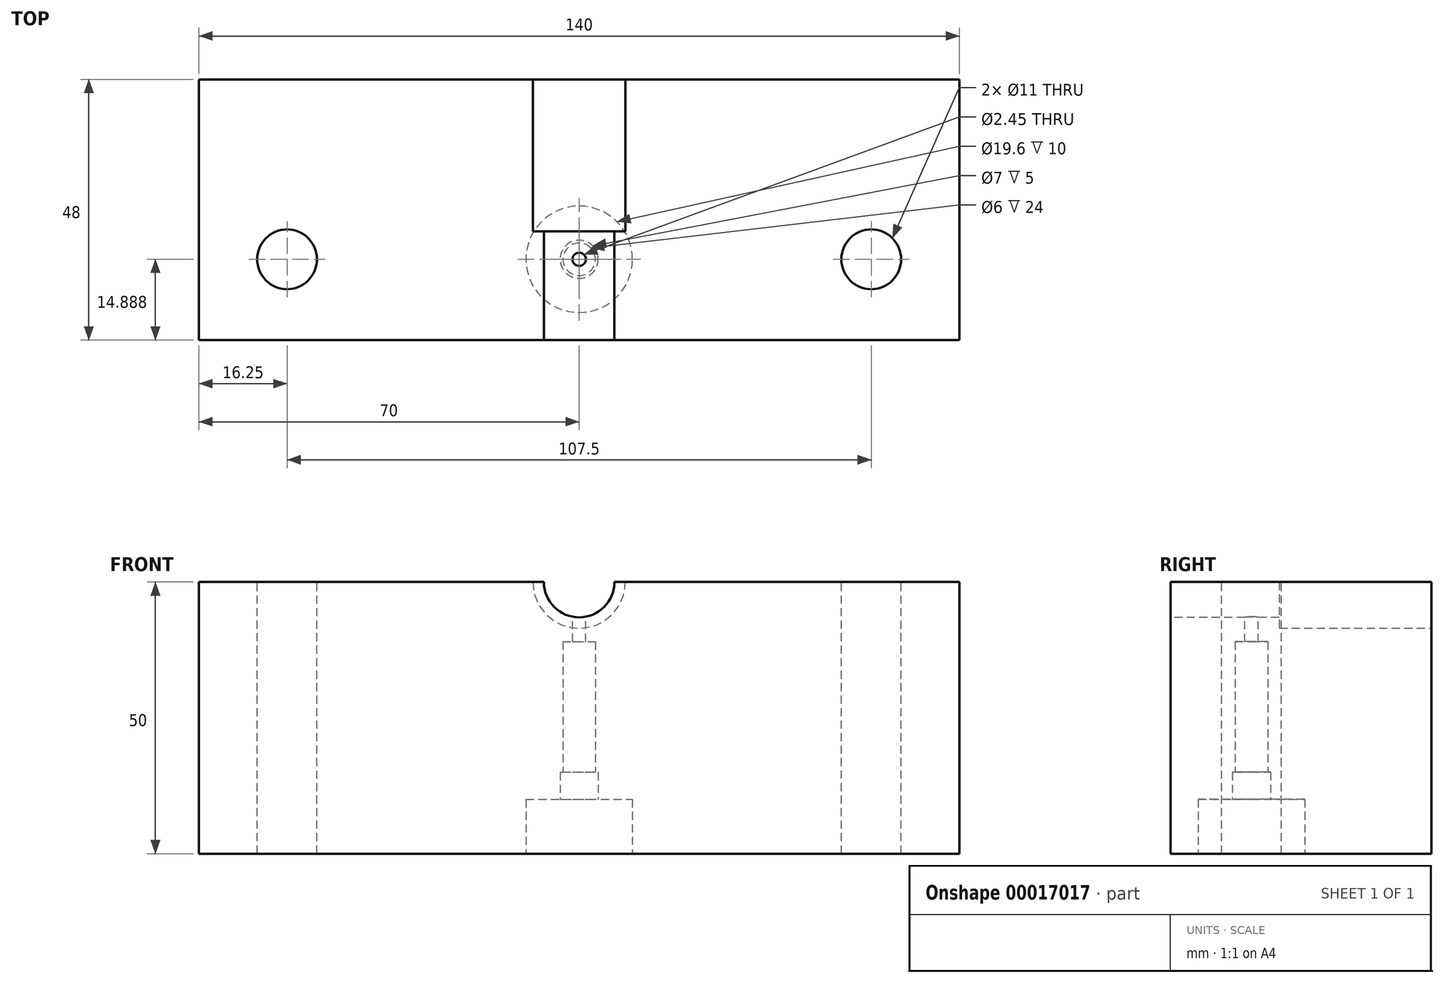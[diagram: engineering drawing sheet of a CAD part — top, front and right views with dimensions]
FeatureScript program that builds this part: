
annotation { "Feature Type Name" : "Feature", "Feature Type Description" : "" }
export const myFeature = defineFeature(function(context is Context, id is Id, definition is map)
    precondition{}
    {
        {
            var Q0;
            Q0=qCreatedBy(makeId("Front.planeOp"),FACE);
            var sketch = newSketch(context, id + "F0", { "sketchPlane" : qUnion([Q0])});
            skLineSegment(sketch, "E0.bottom", {"start": v(0, 0) * mm, "end": v(-140, 0) * mm});
            skLineSegment(sketch, "E0.top", {"start": v(0, 50) * mm, "end": v(-63.5, 50) * mm});
            skLineSegment(sketch, "E0.left", {"start": v(0, 0) * mm, "end": v(0, 50) * mm});
            skLineSegment(sketch, "E0.right", {"start": v(-140, 0) * mm, "end": v(-140, 50) * mm});
            skLineSegment(sketch, "E1.trimOffspring", {"start": v(-76.5, 50) * mm, "end": v(-140, 50) * mm});
            skPoint(sketch, "E2.center.orphan", {"position": v(-70, 50) * mm});
            skLineSegment(sketch, "E3", {"start": v(-63.5, 50) * mm, "end": v(-76.5, 50) * mm});
            skSolve(sketch);
        }
        {
            var Q0;
            Q0=makeQuery(id+"F0.imprint","IMPRINT",FACE,{"disambiguationData":[TD([[makeQuery(id+"F0.imprint","IMPRINT",EDGE,{"derivedFrom":sQuery(id+"F0.wireOp",EDGE,"E0.bottom")}),-1.0]])]});
            extrude(context, id + "F1", {"entities" : qUnion([Q0]), "depth" : 48 * mm});
        }
        {
            var Q0;
            Q0=makeQuery(id+"F1.opExtrude","SWEPT_FACE",FACE,{"disambiguationData":[OSD([sQuery(id+"F0.wireOp",EDGE,"E1.trimOffspring")])]});
            var sketch = newSketch(context, id + "F2", { "sketchPlane" : qUnion([Q0])});
            skCircle(sketch, "E4", {"center": v(-123.75, -33.11) * mm, "radius": 5.5 * mm});
            skCircle(sketch, "E5", {"center": v(-16.25, -33.11) * mm, "radius": 5.5 * mm});
            skSolve(sketch);
        }
        {
            var Q0;
            Q0 = qSketchRegion(id + "F2", true);
            extrude(context, id + "F3", {"entities" : qUnion([Q0]), "operationType" : NewBodyOperationType.REMOVE, "endBound" : BoundingType.THROUGH_ALL, "oppositeDirection" : true, "depth" : 25 * mm});
        }
        {
            var Q0;
            Q0=makeQuery(id+"F1.opExtrude","CAP_FACE",FACE,{"disambiguationData":[OSD([sQuery(id+"F0.wireOp",EDGE,"E0.bottom"),sQuery(id+"F0.wireOp",EDGE,"E0.top"),sQuery(id+"F0.wireOp",EDGE,"E0.left"),sQuery(id+"F0.wireOp",EDGE,"E0.right"),sQuery(id+"F0.wireOp",EDGE,"E1.trimOffspring"),sQuery(id+"F0.wireOp",EDGE,"E3")])],"isStart":false});
            var sketch = newSketch(context, id + "F4", { "sketchPlane" : qUnion([Q0])});
            skCircle(sketch, "E6", {"center": v(-70, 50) * mm, "radius": 6.5 * mm});
            skSolve(sketch);
        }
        {
            var Q0;
            Q0 = qSketchRegion(id + "F4", true);
            extrude(context, id + "F5", {"entities" : qUnion([Q0]), "operationType" : NewBodyOperationType.REMOVE, "oppositeDirection" : true, "depth" : 20 * mm});
        }
        {
            var Q0;
            Q0=makeQuery(id+"F1.opExtrude","CAP_FACE",FACE,{"disambiguationData":[OSD([sQuery(id+"F0.wireOp",EDGE,"E0.bottom"),sQuery(id+"F0.wireOp",EDGE,"E0.top"),sQuery(id+"F0.wireOp",EDGE,"E0.left"),sQuery(id+"F0.wireOp",EDGE,"E0.right"),sQuery(id+"F0.wireOp",EDGE,"E1.trimOffspring"),sQuery(id+"F0.wireOp",EDGE,"E3")])],"isStart":true});
            var sketch = newSketch(context, id + "F6", { "sketchPlane" : qUnion([Q0])});
            skCircle(sketch, "E7", {"center": v(70, 50) * mm, "radius": 8.5 * mm});
            skSolve(sketch);
        }
        {
            var Q0;
            Q0 = qSketchRegion(id + "F6", true);
            extrude(context, id + "F7", {"entities" : qUnion([Q0]), "operationType" : NewBodyOperationType.REMOVE, "oppositeDirection" : true, "depth" : 28 * mm});
        }
        {
            var Q0;
            {var subQ0=sQuery(id+"F0.wireOp",EDGE,"E0.top");var subQ1=sQuery(id+"F0.wireOp",EDGE,"E1.trimOffspring");var subQ2=sQuery(id+"F0.wireOp",EDGE,"E3");var subQ5=sQuery(id+"F0.wireOp",EDGE,"E0.left");Q0=makeQuery(id+"F7.boolean.opBoolean","SPLIT",FACE,{"disambiguationData":[TD([makeQuery(id+"F1.opExtrude","SWEPT_FACE",FACE,{"disambiguationData":[OSD([subQ5])]})])],"derivedFrom":makeQuery(id+"F1.opExtrude","SWEPT_FACE",FACE,{"disambiguationData":[OSD([subQ0,subQ1,subQ2])]})});}
            var sketch = newSketch(context, id + "F8", { "sketchPlane" : qUnion([Q0])});
            skCircle(sketch, "E8", {"center": v(-70, -33.11) * mm, "radius": 1.23 * mm});
            skSolve(sketch);
        }
        {
            var Q0;
            Q0 = qSketchRegion(id + "F8", true);
            extrude(context, id + "F9", {"entities" : qUnion([Q0]), "operationType" : NewBodyOperationType.REMOVE, "endBound" : BoundingType.THROUGH_ALL, "oppositeDirection" : true, "depth" : 25 * mm});
        }
        {
            var Q0;
            Q0=makeQuery(id+"F1.opExtrude","SWEPT_FACE",FACE,{"disambiguationData":[OSD([sQuery(id+"F0.wireOp",EDGE,"E0.bottom")])]});
            var sketch = newSketch(context, id + "F10", { "sketchPlane" : qUnion([Q0])});
            skCircle(sketch, "E9", {"center": v(-70, 33.11) * mm, "radius": 9.8 * mm});
            skSolve(sketch);
        }
        {
            var Q0;
            Q0 = qSketchRegion(id + "F10", true);
            extrude(context, id + "F11", {"entities" : qUnion([Q0]), "operationType" : NewBodyOperationType.REMOVE, "oppositeDirection" : true, "depth" : 10 * mm});
        }
        {
            var Q0;
            Q0=makeQuery(id+"F11.boolean.opBoolean","COPY",FACE,{"derivedFrom":makeQuery(id+"F11.opExtrude","CAP_FACE",FACE,{"disambiguationData":[OSD([sQuery(id+"F10.wireOp",EDGE,"E9")])],"isStart":false})});
            var sketch = newSketch(context, id + "F12", { "sketchPlane" : qUnion([Q0])});
            skCircle(sketch, "E10", {"center": v(-70, 33.11) * mm, "radius": 3.5 * mm});
            skSolve(sketch);
        }
        {
            var Q0;
            Q0=makeQuery(id+"F12.imprint","IMPRINT",FACE,{"disambiguationData":[TD([[makeQuery(id+"F12.imprint","IMPRINT",EDGE,{"derivedFrom":sQuery(id+"F12.wireOp",EDGE,"E10")}),1.0]])]});
            extrude(context, id + "F13", {"entities" : qUnion([Q0]), "operationType" : NewBodyOperationType.REMOVE, "oppositeDirection" : true, "depth" : 5 * mm});
        }
        {
            var Q0;
            Q0=makeQuery(id+"F13.boolean.opBoolean","COPY",FACE,{"derivedFrom":makeQuery(id+"F13.opExtrude","CAP_FACE",FACE,{"disambiguationData":[OSD([sQuery(id+"F8.wireOp",EDGE,"E8"),sQuery(id+"F10.wireOp",EDGE,"E9"),sQuery(id+"F12.wireOp",EDGE,"E10")])],"isStart":false})});
            var sketch = newSketch(context, id + "F14", { "sketchPlane" : qUnion([Q0])});
            skCircle(sketch, "E11", {"center": v(-70, 33.11) * mm, "radius": 3 * mm});
            skSolve(sketch);
        }
        {
            var Q0;
            Q0 = qSketchRegion(id + "F14", true);
            extrude(context, id + "F15", {"entities" : qUnion([Q0]), "operationType" : NewBodyOperationType.REMOVE, "oppositeDirection" : true, "depth" : 24 * mm});
        }
    });
